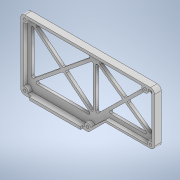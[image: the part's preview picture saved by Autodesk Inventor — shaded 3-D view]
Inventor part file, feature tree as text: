
AUTODESK INVENTOR PART (.ipt)
format: ipt  version: 2021 (Build 250183000, 183)  size: 485,888 bytes
history: native  units: mm
features: sketch x18, extrude x16, fillet x4, hole x2, chamfer x2
ambient origin geometry x8: Origin, YZ Plane, XZ Plane, XY Plane, X Axis, Y Axis, Z Axis, Center Point
bodies: Solid1 (feature_tree)
feature tree (42):
  extrude  "Extrusion1"  Depth=100.0mm
  extrude  "Extrusion2"  Depth=50.0mm
  hole  "Hole1"  [1 undecoded]
  extrude  "Extrusion3"  Depth=50.0mm
  extrude  "Extrusion4"  Depth=3.0mm
  extrude  "Extrusion5"  Depth=3.0mm
  fillet  "Fillet1"  Radius=49.0mm
  extrude  "Extrusion6"  Depth=93.0mm
  extrude  "Extrusion7"  Depth=5.0mm
  extrude  "Extrusion8"  Depth=5.0mm
  chamfer  "Chamfer1"  Distance=3.0mm
  extrude  "Extrusion9"  Depth=12.5mm
  fillet  "Fillet2"  Radius=63.1mm
  extrude  "Extrusion11"  Depth=3.0mm
  extrude  "Extrusion12"  Depth=2.0mm
  chamfer  "Chamfer2"  Distance=2.0mm
  extrude  "Extrusion13"  Depth=2.0mm
  extrude  "Extrusion14"  Depth=1.5mm
  extrude  "Extrusion15"  Depth=3.0mm TaperAngle=0.0deg
  fillet  "Fillet3"  Radius=3.0mm
  fillet  "Fillet4"  Radius=7.6mm
  hole  "Hole2"  [1 undecoded]
  extrude  "Extrusion20"  Depth=2.0mm
  extrude  "Extrusion21"  Depth=3.0mm TaperAngle=0.0deg
  sketch  "Sketch1"  dims[d0=52.0mm d1=100.0mm]
  sketch  "Sketch2"  dims[d2=26.0mm d3=50.0mm]
  sketch  "Sketch3"  dims[d4=2.0mm d5=0.0mm d6=3.0mm]
  sketch  "Sketch4"  dims[d7=3.0mm d8=50.0mm]
  sketch  "Sketch5"  dims[d9=3.0mm d10=97.0mm]
  sketch  "Sketch6"  dims[d11=15.0mm d12=3.0mm d13=49.0mm]
  sketch  "Sketch7"  dims[d14=93.0mm d15=49.0mm]
  sketch  "Sketch8"  dims[d16=2.0mm d17=5.0mm]
  sketch  "Sketch9"  dims[d18=2.0mm d19=5.0mm]
  sketch  "Sketch10"  dims[d20=2.0mm]
  sketch  "Sketch12"  dims[d21=5.0mm]
  sketch  "Sketch13"  dims[d22=2.0mm]
  sketch  "Sketch14"  dims[d23=5.0mm]
  sketch  "Sketch15"  dims[d24=2.0mm]
  sketch  "Sketch16"  dims[d25=5.0mm d26=3.0mm d27=0.0mm]
  sketch  "Sketch17"  dims[d28=2.0mm d29=6.0mm d30=5.0mm d31=2.0mm d32=90.0deg d33=10.0mm d34=20.594885mm d35=12.5mm d36=63.1mm]
  sketch  "Sketch23"  dims[d37=3.0mm d38=0.0mm d39=50.673mm]
  sketch  "Sketch24"  dims[d40=3.0mm d41=0.0mm d42=2.0mm d43=2.0mm d44=2.0mm d45=1.5mm d46=3.0mm d47=0.0mm d48=3.0mm d49=7.6mm d50=46.4mm d51=6.7mm d52=3.0mm d53=0.0mm d54=5.0mm d55=2.0mm d56=12.0mm d57=0.0mm d58=1.4mm d59=1.2mm d60=3.0mm d61=14.0mm d62=1.2mm d63=1.4mm d64=12.0mm d65=3.0mm d66=0.0mm d67=1.0mm d68=2.0mm d69=45.0deg d70=1.2mm d71=3.0mm d72=0.0mm d73=1.0mm d77=3.0mm d78=0.0mm d79=3.0mm d80=3.0mm d81=3.0mm d82=3.0mm d83=3.0mm d84=3.0mm d85=3.0mm d86=48.0mm d87=2.0mm d88=0.0mm d89=8.4mm d90=2.0mm d91=45.0deg d92=1.2mm d93=3.0mm d94=0.0mm d95=7.6mm d96=5.0mm d97=0.0mm d98=2.0mm d99=2.0mm d100=2.0mm d101=2.0mm d102=2.0mm d103=2.0mm d104=0.0mm d105=1.0mm d106=1.0mm d107=2.0mm d108=6.0mm d109=5.0mm d110=2.0mm d111=90.0deg d112=4.0mm d113=20.594885mm d146=6.5mm d147=5.0mm d148=2.0mm d149=0.0mm d150=0.3mm d151=0.3mm d152=2.0mm d153=0.0mm d74=0.872665mm d75=0.872665mm d76=0.5mm d114=0.75mm d115=20.594885mm d116=0.0625mm d117=0.75mm d118=0.375mm]
note: 2 required parameter values undecoded (feature->parameter linkage not recoverable at this tier; creation-order binding heuristic only, values carry confidence <= 0.55)
